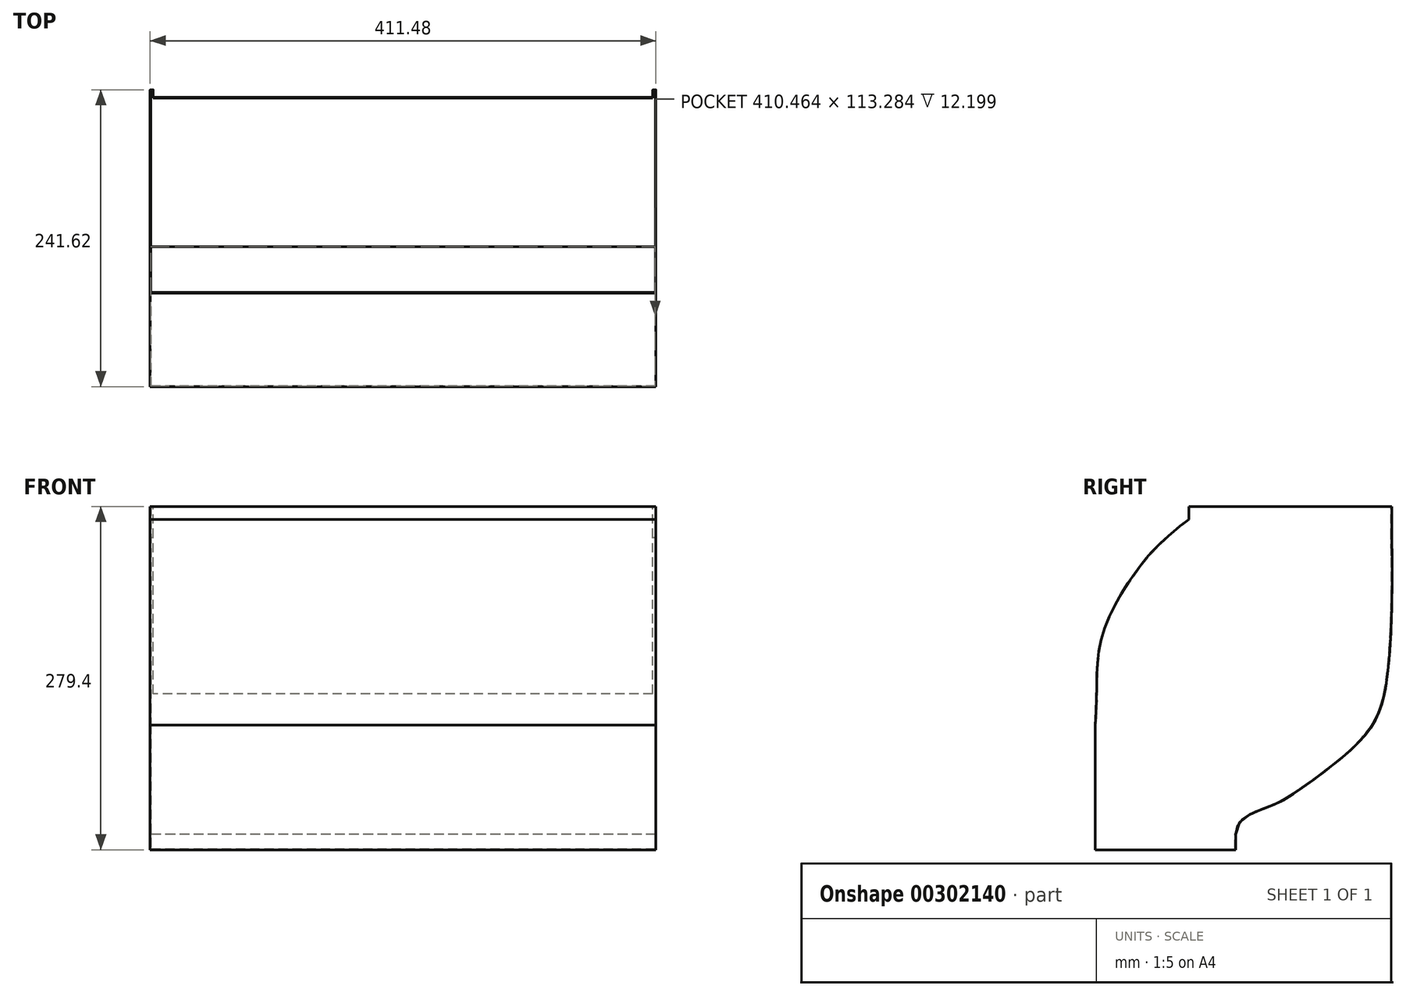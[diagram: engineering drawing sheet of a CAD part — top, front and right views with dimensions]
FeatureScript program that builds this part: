
annotation { "Feature Type Name" : "Feature", "Feature Type Description" : "" }
export const myFeature = defineFeature(function(context is Context, id is Id, definition is map)
    precondition{}
    {
        {
            var Q0;
            Q0=qCreatedBy(makeId("Right.planeOp"),FACE);
            var sketch = newSketch(context, id + "F0", { "sketchPlane" : qUnion([Q0])});
            skLineSegment(sketch, "E0", {"start": v(-141.6, 101.6) * mm, "end": v(-141.6, 0) * mm});
            skLineSegment(sketch, "E1", {"start": v(-141.6, 0) * mm, "end": v(-27.3, 0) * mm});
            skLineSegment(sketch, "E2", {"start": v(-27.3, 0) * mm, "end": v(-27.3, 12.7) * mm});
            skLineSegment(sketch, "E3", {"start": v(99.7, 254) * mm, "end": v(99.7, 279.4) * mm});
            skLineSegment(sketch, "E4", {"start": v(99.7, 279.4) * mm, "end": v(-65.4, 279.4) * mm});
            skLineSegment(sketch, "E5", {"start": v(-65.4, 279.4) * mm, "end": v(-65.4, 268.69) * mm});
            skFitSpline(sketch, "E6", {"points": [v(-65.4, 268.69) * mm, v(-86.98, 250.76) * mm, v(-102.8, 233.77) * mm, v(-136.26, 172.84) * mm, v(-141.6, 101.6) * mm], "startDerivative": vector(-189.95, -139.83) * mm, "endDerivative": vector(-24.56, -262.81) * mm});
            skFitSpline(sketch, "E7", {"points": [v(-27.3, 12.7) * mm, v(0, 35.18) * mm, v(28.4, 51.6) * mm, v(76.44, 91.44) * mm, v(95.23, 135.03) * mm, v(99.7, 254) * mm], "startDerivative": vector(7.37, 271.97) * mm, "endDerivative": vector(-8.41, 387.03) * mm});
            skSolve(sketch);
        }
        {
            var Q0;
            Q0=makeQuery(id+"F0.imprint","IMPRINT",FACE,{"disambiguationData":[TD([[makeQuery(id+"F0.imprint","IMPRINT",EDGE,{"derivedFrom":sQuery(id+"F0.wireOp",EDGE,"E0")}),1.0]])]});
            extrude(context, id + "F1", {"entities" : qUnion([Q0]), "depth" : 411.48 * mm});
        }
        {
            var Q0;
            Q0=makeQuery(id+"F1.opExtrude","SWEPT_FACE",FACE,{"disambiguationData":[OSD([sQuery(id+"F0.wireOp",EDGE,"E4")])]});
            shell(context, id + "F2", {"entities" : qUnion([Q0]), "thickness" : 0.5 * mm});
        }
        {
            var Q0;
            Q0=makeQuery(id+"F1.opExtrude","SWEPT_FACE",FACE,{"disambiguationData":[OSD([sQuery(id+"F0.wireOp",EDGE,"E4")])]});
            var sketch = newSketch(context, id + "F3", { "sketchPlane" : qUnion([Q0])});
            skLineSegment(sketch, "E8.bottom", {"start": v(408.94, 85.28) * mm, "end": v(2.54, 85.28) * mm});
            skLineSegment(sketch, "E8.top", {"start": v(408.94, 117.16) * mm, "end": v(2.54, 117.16) * mm});
            skLineSegment(sketch, "E8.left", {"start": v(408.94, 85.28) * mm, "end": v(408.94, 117.16) * mm});
            skLineSegment(sketch, "E8.right", {"start": v(2.54, 85.28) * mm, "end": v(2.54, 117.16) * mm});
            skSolve(sketch);
        }
        {
            var Q0;
            {var subQ0=sQuery(id+"F3.wireOp",EDGE,"E8.top");Q0=makeQuery(id+"F3.imprint","IMPRINT",FACE,{"disambiguationData":[TD([[makeQuery(id+"F3.imprint","IMPRINT",EDGE,{"derivedFrom":subQ0}),1.0]])]});}
            var Q1;
            {var subQ0=sQuery(id+"F3.wireOp",EDGE,"E8.bottom");Q1=makeQuery(id+"F3.imprint","IMPRINT",FACE,{"disambiguationData":[TD([[makeQuery(id+"F3.imprint","IMPRINT",EDGE,{"derivedFrom":subQ0}),-1.0]])]});}
            var Q2;
            {var subQ0=sQuery(id+"F3.wireOp",EDGE,"E8.left");var subQ1=sQuery(id+"F0.wireOp",EDGE,"E4");var subQ2=sQuery(id+"F0.wireOp",EDGE,"E3");var subQ3=makeQuery(id+"F1.opExtrude","SWEPT_EDGE",EDGE,{"disambiguationData":[OSD([subQ2,subQ1])]});var subQ4=makeQuery(id+"F3.imprint","INTERSECT",VERTEX,{"derivedFrom":[subQ3,subQ0]});Q2=makeQuery(id+"F3.imprint","IMPRINT",FACE,{"disambiguationData":[TD([[makeQuery(id+"F3.imprint","IMPRINT",EDGE,{"disambiguationData":[TD([[subQ4,1.0]])],"derivedFrom":subQ0}),1.0]])]});}
            extrude(context, id + "F4", {"entities" : qUnion([Q0, Q1, Q2]), "operationType" : NewBodyOperationType.REMOVE, "oppositeDirection" : true, "depth" : 152.4 * mm});
        }
    });
